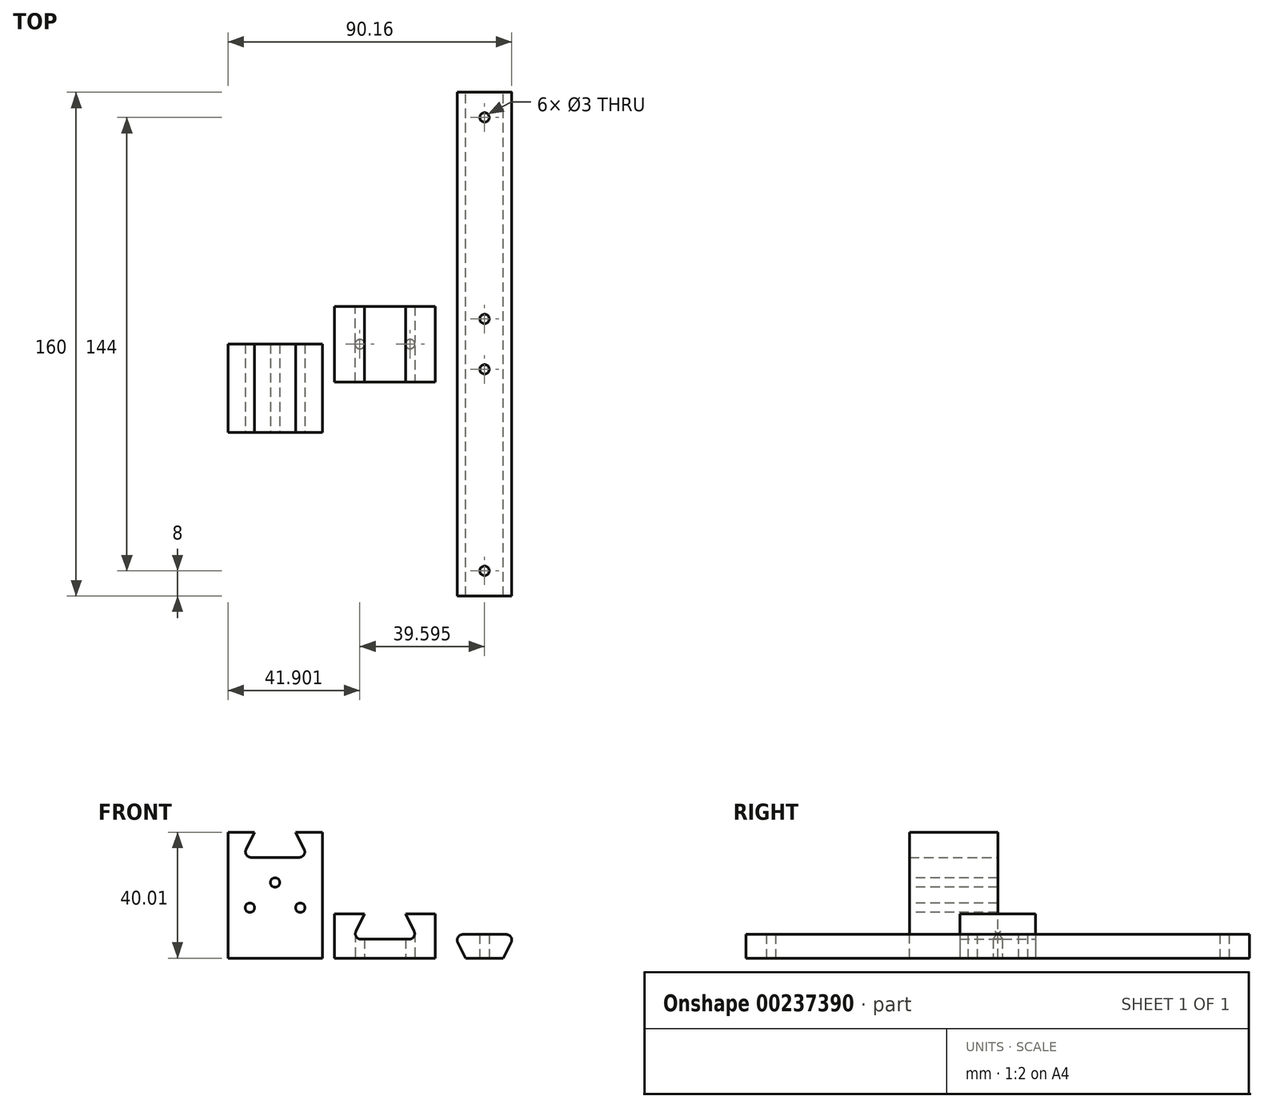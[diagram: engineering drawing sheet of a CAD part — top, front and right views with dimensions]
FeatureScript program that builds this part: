
annotation { "Feature Type Name" : "Feature", "Feature Type Description" : "" }
export const myFeature = defineFeature(function(context is Context, id is Id, definition is map)
    precondition{}
    {
        {
            var Q0;
            Q0=qCreatedBy(makeId("Front.planeOp"),FACE);
            var sketch = newSketch(context, id + "F0", { "sketchPlane" : qUnion([Q0])});
            skLineSegment(sketch, "E0.bottom", {"start": v(19.57, 14) * mm, "end": v(-12.43, 14) * mm});
            skLineSegment(sketch, "E0.top", {"start": v(19.57, 0) * mm, "end": v(-12.43, 0) * mm});
            skLineSegment(sketch, "E0.left", {"start": v(19.57, 14) * mm, "end": v(19.57, 0) * mm});
            skLineSegment(sketch, "E0.right", {"start": v(-12.43, 14) * mm, "end": v(-12.43, 0) * mm});
            skLineSegment(sketch, "E1", {"start": v(10.07, 14) * mm, "end": v(14.07, 6) * mm});
            skLineSegment(sketch, "E2", {"start": v(-2.93, 14) * mm, "end": v(-6.93, 6) * mm});
            skLineSegment(sketch, "E3", {"start": v(14.07, 6) * mm, "end": v(-6.93, 6) * mm});
            skSolve(sketch);
        }
        {
            var Q0;
            Q0=makeQuery(id+"F0.imprint","IMPRINT",FACE,{"disambiguationData":[TD([[makeQuery(id+"F0.imprint","IMPRINT",EDGE,{"derivedFrom":sQuery(id+"F0.wireOp",EDGE,"E0.top")}),-1.0]])]});
            extrude(context, id + "F1", {"entities" : qUnion([Q0]), "endBound" : BoundingType.SYMMETRIC, "depth" : 24 * mm});
        }
        {
            var Q0;
            Q0=qCreatedBy(makeId("Front.planeOp"),FACE);
            var sketch = newSketch(context, id + "F2", { "sketchPlane" : qUnion([Q0])});
            skLineSegment(sketch, "E4.bottom", {"start": v(25.17, 0) * mm, "end": v(45.17, 0) * mm});
            skLineSegment(sketch, "E4.top", {"start": v(25.17, 8) * mm, "end": v(45.17, 8) * mm});
            skLineSegment(sketch, "E4.left", {"start": v(25.17, 0) * mm, "end": v(25.17, 8) * mm});
            skLineSegment(sketch, "E4.right", {"start": v(45.17, 0) * mm, "end": v(45.17, 8) * mm});
            skLineSegment(sketch, "E5", {"start": v(25.17, 8) * mm, "end": v(29.17, 0) * mm});
            skLineSegment(sketch, "E6", {"start": v(45.17, 8) * mm, "end": v(41.17, 0) * mm});
            skLineSegment(sketch, "E7.left", {"start": v(25.17, 8) * mm, "end": v(25.17, 8) * mm});
            skLineSegment(sketch, "E7.right", {"start": v(45.17, 8) * mm, "end": v(45.17, 8) * mm});
            skLineSegment(sketch, "E8.top", {"start": v(25.17, 7.5) * mm, "end": v(45.17, 7.5) * mm});
            skLineSegment(sketch, "E8.left", {"start": v(25.17, 8) * mm, "end": v(25.17, 7.5) * mm});
            skLineSegment(sketch, "E8.right", {"start": v(45.17, 8) * mm, "end": v(45.17, 7.5) * mm});
            skSolve(sketch);
        }
        {
            var Q0;
            {var subQ0=sQuery(id+"F2.wireOp",EDGE,"E5");var subQ1=sQuery(id+"F2.wireOp",EDGE,"E4.bottom");var subQ2=makeQuery(id+"F2.imprint","INTERSECT",VERTEX,{"derivedFrom":[subQ1,subQ0]});Q0=makeQuery(id+"F2.imprint","IMPRINT",FACE,{"disambiguationData":[TD([[makeQuery(id+"F2.imprint","IMPRINT",EDGE,{"disambiguationData":[TD([[subQ2,-1.0]])],"derivedFrom":subQ1}),1.0]])]});}
            extrude(context, id + "F3", {"entities" : qUnion([Q0]), "endBound" : BoundingType.SYMMETRIC, "depth" : 160 * mm});
        }
        {
            var Q0;
            Q0=makeQuery(id+"F1.opExtrude","SWEPT_FACE",FACE,{"disambiguationData":[OSD([sQuery(id+"F0.wireOp",EDGE,"E0.top")])]});
            var sketch = newSketch(context, id + "F4", { "sketchPlane" : qUnion([Q0])});
            skPoint(sketch, "E9.centerSnap0", {"position": v(19.57, 0) * mm});
            skCircle(sketch, "E10", {"center": v(-4.43, 0) * mm, "radius": 1.5 * mm});
            skCircle(sketch, "E11.1.0.0", {"center": v(11.57, 0) * mm, "radius": 1.5 * mm});
            skLineSegment(sketch, "E11.direction1", {"start": v(-4.43, 0) * mm, "end": v(11.57, 0) * mm, "construction": true});
            skSolve(sketch);
        }
        {
            var Q0;
            Q0=makeQuery(id+"F4.imprint","IMPRINT",FACE,{"disambiguationData":[TD([[makeQuery(id+"F4.imprint","IMPRINT",EDGE,{"derivedFrom":sQuery(id+"F4.wireOp",EDGE,"E10")}),1.0]])]});
            var Q1;
            Q1=makeQuery(id+"F4.imprint","IMPRINT",FACE,{"disambiguationData":[TD([[makeQuery(id+"F4.imprint","IMPRINT",EDGE,{"derivedFrom":sQuery(id+"F4.wireOp",EDGE,"E11.1.0.0")}),1.0]])]});
            extrude(context, id + "F5", {"entities" : qUnion([Q0, Q1]), "operationType" : NewBodyOperationType.REMOVE, "oppositeDirection" : true, "depth" : 7 * mm});
        }
        {
            var Q0;
            Q0=makeQuery(id+"F3.opExtrude","SWEPT_FACE",FACE,{"disambiguationData":[OSD([sQuery(id+"F2.wireOp",EDGE,"E4.bottom")])]});
            var sketch = newSketch(context, id + "F6", { "sketchPlane" : qUnion([Q0])});
            skCircle(sketch, "E12", {"center": v(35.17, -72) * mm, "radius": 1.5 * mm});
            skCircle(sketch, "E13.0.1.0", {"center": v(35.17, 72) * mm, "radius": 1.5 * mm});
            skCircle(sketch, "E14.0.1.0", {"center": v(35.17, 8) * mm, "radius": 1.5 * mm});
            skCircle(sketch, "E15", {"center": v(35.17, -8) * mm, "radius": 1.5 * mm});
            skSolve(sketch);
        }
        {
            var Q0;
            Q0=makeQuery(id+"F6.imprint","IMPRINT",FACE,{"disambiguationData":[TD([[makeQuery(id+"F6.imprint","IMPRINT",EDGE,{"derivedFrom":sQuery(id+"F6.wireOp",EDGE,"E13.0.1.0")}),1.0]])]});
            var Q1;
            Q1=makeQuery(id+"F6.imprint","IMPRINT",FACE,{"disambiguationData":[TD([[makeQuery(id+"F6.imprint","IMPRINT",EDGE,{"derivedFrom":sQuery(id+"F6.wireOp",EDGE,"E12")}),1.0]])]});
            var Q2;
            Q2=makeQuery(id+"F6.imprint","IMPRINT",FACE,{"disambiguationData":[TD([[makeQuery(id+"F6.imprint","IMPRINT",EDGE,{"derivedFrom":sQuery(id+"F6.wireOp",EDGE,"E14.0.1.0")}),1.0]])]});
            var Q3;
            Q3=makeQuery(id+"F6.imprint","IMPRINT",FACE,{"disambiguationData":[TD([[makeQuery(id+"F6.imprint","IMPRINT",EDGE,{"derivedFrom":sQuery(id+"F6.wireOp",EDGE,"E15")}),1.0]])]});
            extrude(context, id + "F7", {"entities" : qUnion([Q0, Q1, Q2, Q3]), "operationType" : NewBodyOperationType.REMOVE, "endBound" : BoundingType.THROUGH_ALL, "oppositeDirection" : true, "depth" : 25 * mm});
        }
        {
            var Q0;
            Q0=qCreatedBy(makeId("Front.planeOp"),FACE);
            var sketch = newSketch(context, id + "F8", { "sketchPlane" : qUnion([Q0])});
            skLineSegment(sketch, "E16.bottom", {"start": v(-46.33, 0) * mm, "end": v(-16.33, 0) * mm});
            skLineSegment(sketch, "E16.top", {"start": v(-46.33, 40) * mm, "end": v(-16.33, 40) * mm});
            skLineSegment(sketch, "E16.left", {"start": v(-46.33, 0) * mm, "end": v(-46.33, 40) * mm});
            skLineSegment(sketch, "E16.right", {"start": v(-16.33, 0) * mm, "end": v(-16.33, 40) * mm});
            skLineSegment(sketch, "E17", {"start": v(-37.83, 40) * mm, "end": v(-41.83, 32) * mm});
            skLineSegment(sketch, "E18", {"start": v(-41.83, 32) * mm, "end": v(-20.83, 32) * mm});
            skLineSegment(sketch, "E19", {"start": v(-20.83, 32) * mm, "end": v(-24.83, 40) * mm});
            skSolve(sketch);
        }
        {
            var Q0;
            Q0=makeQuery(id+"F8.imprint","IMPRINT",FACE,{"disambiguationData":[TD([[makeQuery(id+"F8.imprint","IMPRINT",EDGE,{"derivedFrom":sQuery(id+"F8.wireOp",EDGE,"E16.bottom")}),1.0]])]});
            extrude(context, id + "F9", {"entities" : qUnion([Q0]), "depth" : 28 * mm});
        }
        {
            var Q0;
            Q0=makeQuery(id+"F1.opExtrude","SWEPT_EDGE",EDGE,{"disambiguationData":[OSD([sQuery(id+"F0.wireOp",EDGE,"E2"),sQuery(id+"F0.wireOp",EDGE,"E3")])]});
            var Q1;
            Q1=makeQuery(id+"F1.opExtrude","SWEPT_EDGE",EDGE,{"disambiguationData":[OSD([sQuery(id+"F0.wireOp",EDGE,"E1"),sQuery(id+"F0.wireOp",EDGE,"E3")])]});
            var Q2;
            Q2=makeQuery(id+"F3.opExtrude","SWEPT_EDGE",EDGE,{"disambiguationData":[OSD([sQuery(id+"F2.wireOp",EDGE,"E5"),sQuery(id+"F2.wireOp",EDGE,"E8.top")])]});
            var Q3;
            Q3=makeQuery(id+"F3.opExtrude","SWEPT_EDGE",EDGE,{"disambiguationData":[OSD([sQuery(id+"F2.wireOp",EDGE,"E6"),sQuery(id+"F2.wireOp",EDGE,"E8.top")])]});
            var Q4;
            Q4=makeQuery(id+"F9.opExtrude","SWEPT_EDGE",EDGE,{"disambiguationData":[OSD([sQuery(id+"F8.wireOp",EDGE,"E17"),sQuery(id+"F8.wireOp",EDGE,"E18")])]});
            var Q5;
            Q5=makeQuery(id+"F9.opExtrude","SWEPT_EDGE",EDGE,{"disambiguationData":[OSD([sQuery(id+"F8.wireOp",EDGE,"E18"),sQuery(id+"F8.wireOp",EDGE,"E19")])]});
            fillet(context, id + "F10", {"entities" : qUnion([Q0, Q1, Q2, Q3, Q4, Q5]), "radius" : 1.75 * mm, "tangentPropagation" : true, "allowEdgeOverflow" : false});
        }
        {
            var Q0;
            Q0=makeQuery(id+"F9.opExtrude","CAP_FACE",FACE,{"disambiguationData":[OSD([sQuery(id+"F8.wireOp",EDGE,"E16.bottom"),sQuery(id+"F8.wireOp",EDGE,"E16.top"),sQuery(id+"F8.wireOp",EDGE,"E16.left"),sQuery(id+"F8.wireOp",EDGE,"E16.right"),sQuery(id+"F8.wireOp",EDGE,"E17"),sQuery(id+"F8.wireOp",EDGE,"E18"),sQuery(id+"F8.wireOp",EDGE,"E19")])],"isStart":false});
            var sketch = newSketch(context, id + "F11", { "sketchPlane" : qUnion([Q0])});
            skCircle(sketch, "E20", {"center": v(-31.33, 8) * mm, "radius": 1.5 * mm});
            skCircle(sketch, "E21.0.1.0", {"center": v(-31.33, 24) * mm, "radius": 1.5 * mm});
            skLineSegment(sketch, "E21.direction1", {"start": v(-31.33, 8) * mm, "end": v(41, 8) * mm, "construction": true});
            skLineSegment(sketch, "E21.direction2", {"start": v(-31.33, 8) * mm, "end": v(-31.33, 24) * mm, "construction": true});
            skCircle(sketch, "E22.1.0", {"center": v(-23.33, 16) * mm, "radius": 1.5 * mm});
            skCircle(sketch, "E22.1.1", {"center": v(-39.33, 16) * mm, "radius": 1.5 * mm});
            skPoint(sketch, "E22.center", {"position": v(-31.33, 16) * mm});
            skLineSegment(sketch, "E22.anchor1", {"start": v(-31.33, 16) * mm, "end": v(-31.33, 8) * mm, "construction": true});
            skLineSegment(sketch, "E22.anchor2", {"start": v(-31.33, 16) * mm, "end": v(-31.33, 24) * mm, "construction": true});
            skSolve(sketch);
        }
        {
            var Q0;
            Q0=makeQuery(id+"F11.imprint","IMPRINT",FACE,{"disambiguationData":[TD([[makeQuery(id+"F11.imprint","IMPRINT",EDGE,{"derivedFrom":sQuery(id+"F11.wireOp",EDGE,"E21.0.1.0")}),1.0]])]});
            var Q1;
            Q1=makeQuery(id+"F11.imprint","IMPRINT",FACE,{"disambiguationData":[TD([[makeQuery(id+"F11.imprint","IMPRINT",EDGE,{"derivedFrom":sQuery(id+"F11.wireOp",EDGE,"E22.1.0")}),1.0]])]});
            var Q2;
            Q2=makeQuery(id+"F11.imprint","IMPRINT",FACE,{"disambiguationData":[TD([[makeQuery(id+"F11.imprint","IMPRINT",EDGE,{"derivedFrom":sQuery(id+"F11.wireOp",EDGE,"E20")}),1.0]])]});
            var Q3;
            Q3=makeQuery(id+"F11.imprint","IMPRINT",FACE,{"disambiguationData":[TD([[makeQuery(id+"F11.imprint","IMPRINT",EDGE,{"derivedFrom":sQuery(id+"F11.wireOp",EDGE,"E22.1.1")}),1.0]])]});
            extrude(context, id + "F12", {"entities" : qUnion([Q0, Q1, Q2, Q3]), "operationType" : NewBodyOperationType.REMOVE, "endBound" : BoundingType.THROUGH_ALL, "oppositeDirection" : true, "depth" : 25 * mm});
        }
    });
